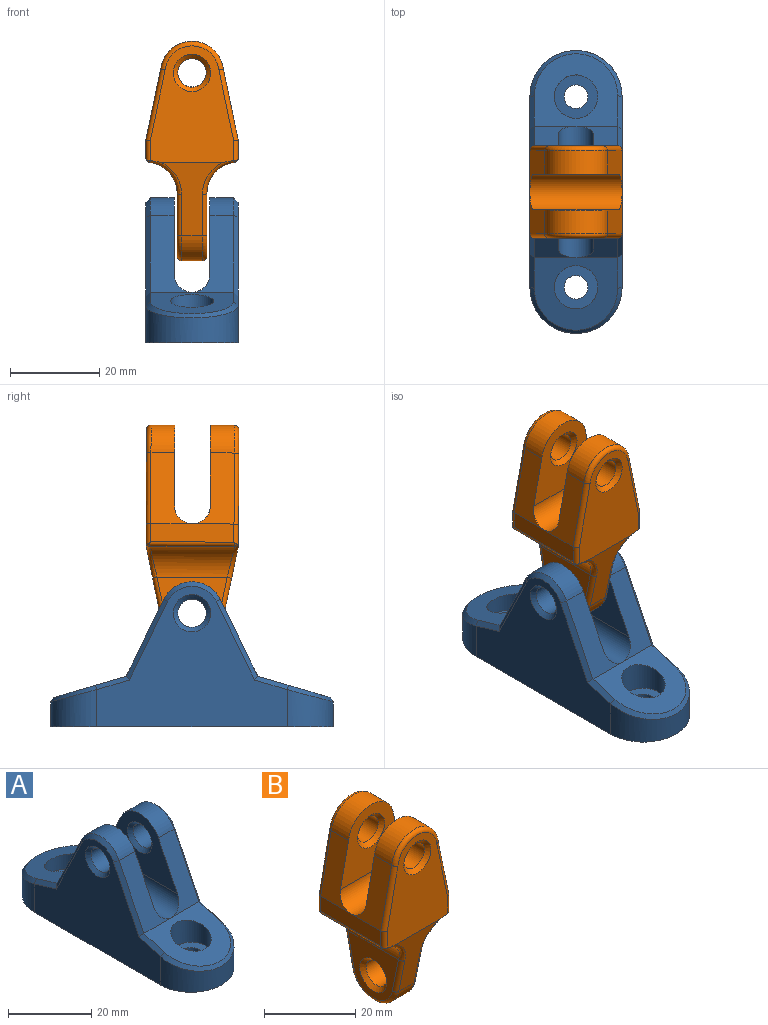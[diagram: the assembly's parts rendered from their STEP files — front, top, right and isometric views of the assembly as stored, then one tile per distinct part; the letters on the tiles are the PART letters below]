
ASSEMBLY  parts=2 mates=1
PART A: 40 faces, bbox 24.6x67.4x36.5 mm
  f0: plane 22.58x20.16mm, normal (0,0.28,0.96), area 200.4mm2, adj f1,f8,f16,f24,f26,f28
  f1: plane 18.07x10.17mm, normal (0,0.9,0.44), area 106.5mm2, adj f0,f2,f5,f21,f22
  f2: cylinder r=7.06mm len=12.7mm, axis (1,0,0), area 84.5mm2, adj f1,f3,f5,f23
  f3: plane 18.07x10.17mm, normal (0,-0.9,0.44), area 106.5mm2, adj f2,f4,f5,f21,f25
  f4: plane 22.58x20.16mm, normal (0,-0.28,0.96), area 200.5mm2, adj f3,f10,f13,f27,f29,f31
  f5: plane 25.61x17.23mm, normal (-1,0,0), area 234.6mm2, adj f1,f2,f3,f21,f37
  f6: plane 42.8x31.58mm, normal (1,0,0), area 749.5mm2, adj f12,f19,f20,f22,f23,f24,f25,f27
  f7: plane 25.61x17.23mm, normal (1,0,0), area 234.6mm2, adj f8,f9,f10,f21,f38
  f8: plane 18.07x10.17mm, normal (0,0.9,0.44), area 106.5mm2, adj f0,f7,f9,f21,f30
  f9: cylinder r=7.06mm len=12.7mm, axis (-1,0,0), area 84.5mm2, adj f7,f8,f10,f32
  f10: plane 18.07x10.17mm, normal (0,-0.9,0.44), area 106.5mm2, adj f4,f7,f9,f21,f33
  f11: plane 42.8x31.58mm, normal (-1,0,0), area 749.5mm2, adj f12,f19,f20,f28,f30,f31,f32,f33
  f12: plane 63.5x20.7mm, normal (0,0,-1), area 1178.4mm2, adj f6,f11,f14,f17,f19,f20
  f13: cylinder r=4.88mm len=9.75mm, axis (0,0,1), area 187.2mm2, adj f4,f15
  f14: cylinder r=2.65mm len=5.3mm, axis (0,0,1), area 66.6mm2, adj f12,f15
  f15: plane 9.75x9.75mm, normal (0,0,1), area 52.6mm2, adj f13,f14
  f16: cylinder r=4.88mm len=9.75mm, axis (0,0,1), area 187.2mm2, adj f0,f18
  f17: cylinder r=2.65mm len=5.3mm, axis (0,0,1), area 66.6mm2, adj f12,f18
  f18: plane 9.75x9.75mm, normal (0,0,1), area 52.6mm2, adj f16,f17
  f19: cylinder r=10.35mm len=20.7mm, axis (0,0,1), area 271.6mm2, adj f6,f11,f12,f29
  f20: cylinder r=10.35mm len=20.7mm, axis (0,0,-1), area 271.6mm2, adj f6,f11,f12,f26
  f21: cylinder r=4mm len=29.5mm, axis (0,-1,0), area 346.2mm2, adj f1,f3,f5,f7,f8,f10
  f22: plane 18.09x9.3mm, normal (0.71,0.64,0.31), area 27.5mm2, adj f1,f6,f23,f24
  f23: cone r=6.06mm half-angle=45deg, axis (-1,0,0), area 20.7mm2, adj f2,f6,f22,f25
  f24: plane 7.64x3mm, normal (0.71,0.2,0.68), area 10.5mm2, adj f0,f6,f22,f26
  f25: plane 18.09x9.3mm, normal (0.71,-0.64,0.31), area 27.5mm2, adj f3,f6,f23,f27
  f26: bspline ~20.7x10.35mm, area 40.4mm2, adj f0,f20,f24,f28
  f27: plane 7.64x3mm, normal (0.71,-0.2,0.68), area 10.5mm2, adj f4,f6,f25,f29
  f28: plane 7.64x3mm, normal (-0.71,0.2,0.68), area 10.5mm2, adj f0,f11,f26,f30
  f29: bspline ~20.7x10.35mm, area 40.4mm2, adj f4,f19,f27,f31
  f30: plane 18.09x9.3mm, normal (-0.71,0.64,0.31), area 27.5mm2, adj f8,f11,f28,f32
  f31: plane 7.64x3mm, normal (-0.71,-0.2,0.68), area 10.5mm2, adj f4,f11,f29,f33
  f32: cone r=7.06mm half-angle=45deg, axis (1,0,0), area 20.7mm2, adj f9,f11,f30,f33
  f33: plane 18.09x9.3mm, normal (-0.71,-0.64,0.31), area 27.5mm2, adj f10,f11,f31,f32
  f34: cylinder r=3.2mm len=6.4mm, axis (1,0,0), area 87.5mm2, adj f36,f38
  f35: cylinder r=3.2mm len=6.4mm, axis (1,0,0), area 87.5mm2, adj f37,f39
  f36: cone r=3.2mm half-angle=45deg, axis (-1,0,0), area 32.9mm2, adj f11,f34
  f37: cone r=4.2mm half-angle=45deg, axis (-1,0,0), area 32.9mm2, adj f5,f35
  f38: cone r=4.2mm half-angle=45deg, axis (1,0,0), area 32.9mm2, adj f7,f34
  f39: cone r=3.2mm half-angle=45deg, axis (1,0,0), area 32.9mm2, adj f6,f35
PART B: 55 faces, bbox 21.4x21.4x50.8 mm
  f0: plane 16.26x9.7mm, normal (0.98,0,0.21), area 90.5mm2, adj f2,f3,f17,f20,f36
  f1: plane 16.29x9.7mm, normal (-0.98,0,0.21), area 90.6mm2, adj f2,f4,f17,f20,f40
  f2: cylinder r=7.06mm len=14.02mm, axis (0,1,0), area 109.5mm2, adj f0,f1,f17,f38
  f3: plane 18.7x4.06mm, normal (1,0,0), area 76mm2, adj f0,f13,f30,f32,f34
  f4: plane 18.7x4.06mm, normal (-1,0,0), area 76mm2, adj f1,f14,f35,f37,f39
  f5: plane 16.51x13.74mm, normal (0,0.98,-0.2), area 98.1mm2, adj f8,f10,f45,f46,f52,f53
  f6: plane 16.51x13.74mm, normal (0,-0.98,-0.2), area 98.1mm2, adj f8,f9,f42,f43,f49,f50
  f7: cylinder r=3.2mm len=6.4mm, axis (-1,0,0), area 94.5mm2, adj f23,f24
  f8: cylinder r=7.06mm len=13.83mm, axis (-1,0,0), area 90.7mm2, adj f5,f6,f44,f51
  f9: plane 26.13x18.7mm, normal (0,-1,0), area 328.5mm2, adj f6,f25,f34,f36,f38,f39,f40,f42
  f10: plane 26.13x18.7mm, normal (0,1,0), area 328.5mm2, adj f5,f28,f29,f30,f31,f33,f35,f46
  f11: plane 15.74x14.13mm, normal (-1,0,0), area 115.9mm2, adj f22,f24,f43,f44,f45
  f12: plane 15.74x14.13mm, normal (1,0,0), area 115.9mm2, adj f21,f23,f50,f51,f52
  f13: plane 16.26x9.7mm, normal (0.98,0,0.21), area 90.5mm2, adj f3,f15,f16,f20,f29
  f14: plane 16.29x9.7mm, normal (-0.98,0,0.21), area 90.6mm2, adj f4,f15,f16,f20,f33
  f15: cylinder r=7.06mm len=14.02mm, axis (0,1,0), area 109.5mm2, adj f13,f14,f16,f31
  f16: plane 19.02x18.13mm, normal (0,-1,0), area 207.9mm2, adj f13,f14,f15,f20,f26
  f17: plane 19.02x18.13mm, normal (0,1,0), area 207.9mm2, adj f0,f1,f2,f20,f27
  f18: cylinder r=3.2mm len=6.4mm, axis (0,-1,0), area 87.5mm2, adj f25,f27
  f19: cylinder r=3.2mm len=6.4mm, axis (0,-1,0), area 87.5mm2, adj f26,f28
  f20: cylinder r=4mm len=20.7mm, axis (1,0,0), area 249.6mm2, adj f0,f1,f13,f14,f16,f17
  f21: cylinder r=7mm len=19.05mm, axis (0,-1,0), area 176mm2, adj f12,f32,f49,f53
  f22: cylinder r=7mm len=19.05mm, axis (0,1,0), area 176mm2, adj f11,f37,f42,f46
  f23: cone r=4.2mm half-angle=45deg, axis (1,0,0), area 32.9mm2, adj f7,f12
  f24: cone r=3.2mm half-angle=45deg, axis (-1,0,0), area 32.9mm2, adj f7,f11
  f25: cone r=3.2mm half-angle=45deg, axis (0,-1,0), area 32.9mm2, adj f9,f18
  f26: cone r=3.2mm half-angle=45deg, axis (0,-1,0), area 32.9mm2, adj f16,f19
  f27: cone r=4.2mm half-angle=45deg, axis (0,1,0), area 32.9mm2, adj f17,f18
  f28: cone r=3.2mm half-angle=45deg, axis (0,1,0), area 32.9mm2, adj f10,f19
  f29: cylinder r=1mm len=16.16mm, axis (0.21,0,-0.98), area 25.5mm2, adj f10,f13,f30,f31
  f30: cylinder r=1mm len=4.63mm, axis (0,0,1), area 6.9mm2, adj f3,f10,f29,f32,f53,f54
  f31: torus R=6.06mm, axis (0,1,0), area 30.6mm2, adj f10,f15,f29,f33
  f32: cylinder r=1mm len=19.05mm, axis (0,-1,0), area 27.5mm2, adj f3,f21,f30,f34,f48,f54
  f33: cylinder r=1mm len=16.19mm, axis (0.21,0,0.98), area 25.5mm2, adj f10,f14,f31,f35
  f34: cylinder r=1mm len=4.63mm, axis (0,0,-1), area 6.9mm2, adj f3,f9,f32,f36,f48,f49
  f35: cylinder r=1mm len=4.63mm, axis (0,0,-1), area 6.9mm2, adj f4,f10,f33,f37,f46,f47
  f36: cylinder r=1mm len=16.16mm, axis (-0.21,0,0.98), area 25.5mm2, adj f0,f9,f34,f38
  f37: cylinder r=1mm len=19.05mm, axis (0,1,0), area 27.5mm2, adj f4,f22,f35,f39,f41,f47
  f38: torus R=6.06mm, axis (0,1,0), area 30.6mm2, adj f2,f9,f36,f40
  f39: cylinder r=1mm len=4.63mm, axis (0,0,1), area 6.9mm2, adj f4,f9,f37,f40,f41,f42
  f40: cylinder r=1mm len=16.19mm, axis (-0.21,0,-0.98), area 25.5mm2, adj f1,f9,f38,f39
  f41: sphere r=1mm, area 0.5mm2, adj f37,f39,f42
  f42: bspline ~7.94x7.13mm, area 15mm2, adj f6,f9,f22,f39,f41,f43
  f43: cylinder r=1mm len=9.51mm, axis (0,-0.2,0.98), area 14.9mm2, adj f6,f11,f42,f44
  f44: torus R=6.06mm, axis (-1,0,0), area 28.7mm2, adj f8,f11,f43,f45
  f45: cylinder r=1mm len=9.51mm, axis (0,-0.2,-0.98), area 14.9mm2, adj f5,f11,f44,f46
  f46: bspline ~9.39x8mm, area 15mm2, adj f5,f10,f22,f35,f45,f47
  f47: sphere r=1mm, area 0.5mm2, adj f35,f37,f46
  f48: sphere r=1mm, area 0.5mm2, adj f32,f34,f49
  f49: bspline ~9.39x8mm, area 15mm2, adj f6,f9,f21,f34,f48,f50
  f50: cylinder r=1mm len=9.51mm, axis (0,-0.2,0.98), area 14.9mm2, adj f6,f12,f49,f51
  f51: torus R=6.06mm, axis (1,0,0), area 28.7mm2, adj f8,f12,f50,f52
  f52: cylinder r=1mm len=9.51mm, axis (0,-0.2,-0.98), area 14.9mm2, adj f5,f12,f51,f53
  f53: bspline ~8.35x8.35mm, area 15mm2, adj f5,f10,f21,f30,f52,f54
  f54: sphere r=1mm, area 0.5mm2, adj f30,f32,f53
PLACE A at identity fixed
PLACE B rot(axis=(1,0,0),0.2deg) t=(0,0.1,-0.05)mm
MATE revolute B.f7 <-> A.f2  axis (1,0,0) through (2.35,0,25.51)mm
